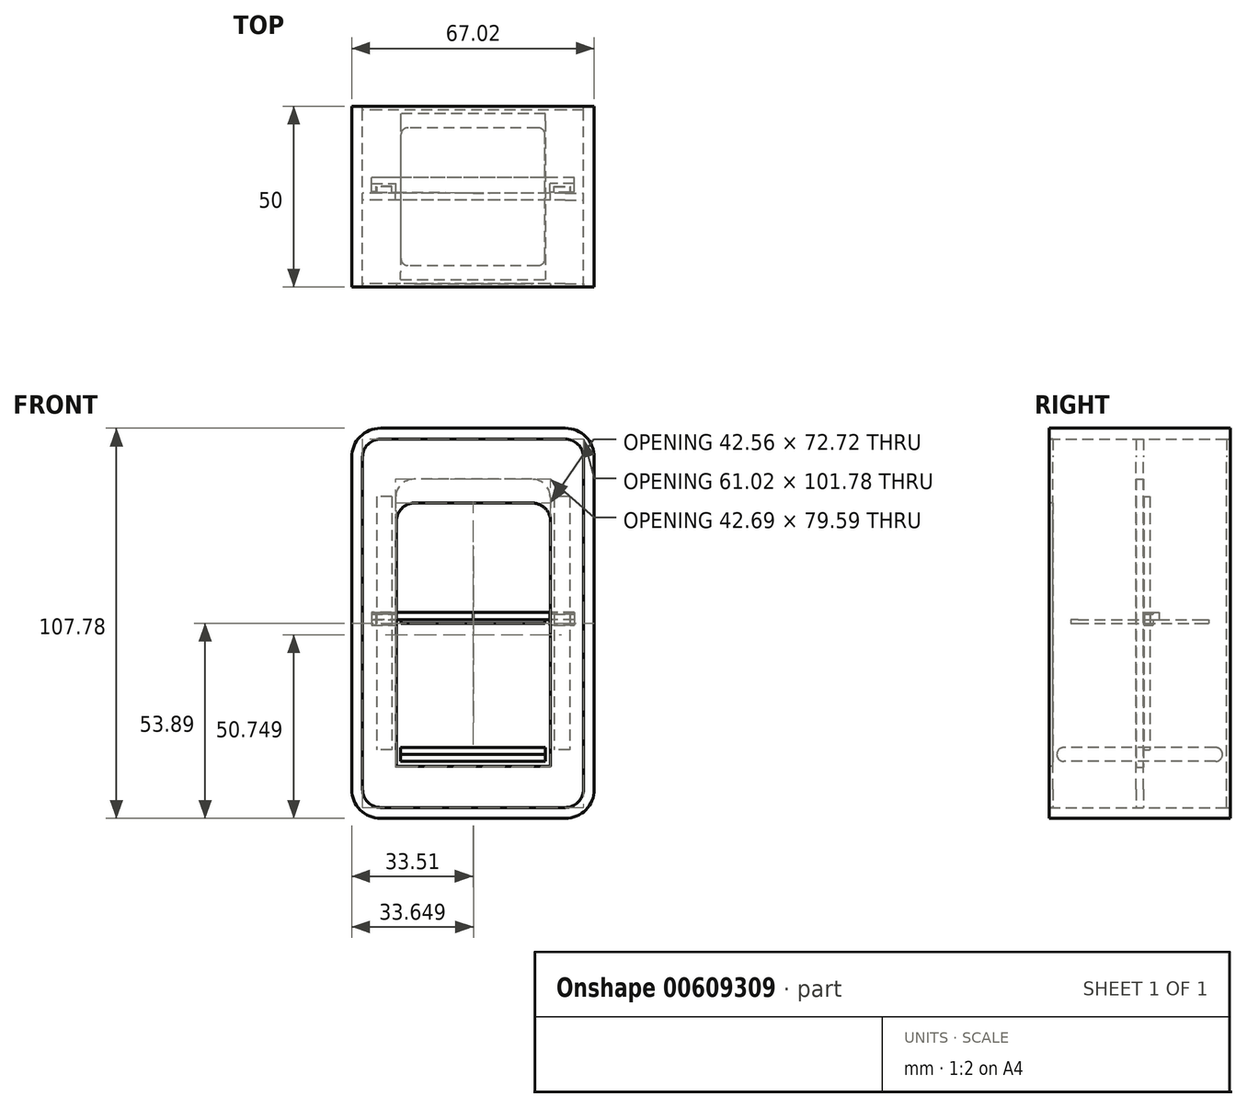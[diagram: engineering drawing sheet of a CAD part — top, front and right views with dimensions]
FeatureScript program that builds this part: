
annotation { "Feature Type Name" : "Feature", "Feature Type Description" : "" }
export const myFeature = defineFeature(function(context is Context, id is Id, definition is map)
    precondition{}
    {
        {
            var Q0;
            Q0=qCreatedBy(makeId("Front.planeOp"),FACE);
            var sketch = newSketch(context, id + "F0", { "sketchPlane" : qUnion([Q0])});
            skLineSegment(sketch, "E0.bottom", {"start": v(25.51, -50.9) * mm, "end": v(-25.51, -50.9) * mm});
            skLineSegment(sketch, "E0.top", {"start": v(25.51, 50.9) * mm, "end": v(-25.51, 50.9) * mm});
            skLineSegment(sketch, "E0.left", {"start": v(30.51, -45.9) * mm, "end": v(30.51, 45.9) * mm});
            skLineSegment(sketch, "E0.right", {"start": v(-30.51, -45.9) * mm, "end": v(-30.51, 45.9) * mm});
            skPoint(sketch, "E0.middle", {"position": v(0, 0) * mm});
            skLineSegment(sketch, "E1.bottom", {"start": v(16.35, 39.8) * mm, "end": v(-16.35, 39.8) * mm});
            skLineSegment(sketch, "E1.top", {"start": v(21.35, -39.8) * mm, "end": v(-21.35, -39.8) * mm});
            skLineSegment(sketch, "E1.left", {"start": v(21.35, 34.8) * mm, "end": v(21.35, -39.8) * mm});
            skLineSegment(sketch, "E1.right", {"start": v(-21.35, 34.8) * mm, "end": v(-21.35, -39.8) * mm});
            skPoint(sketch, "E2.visualSharp", {"position": v(-30.51, 50.9) * mm});
            skArc(sketch, "E2.filletArc", {"start": v(-25.51, 50.9) * mm, "mid": v(-29.05, 49.43) * mm, "end": v(-30.51, 45.9) * mm});
            skPoint(sketch, "E3.visualSharp", {"position": v(30.51, 50.9) * mm});
            skArc(sketch, "E3.filletArc", {"start": v(30.51, 45.9) * mm, "mid": v(29.05, 49.43) * mm, "end": v(25.51, 50.9) * mm});
            skPoint(sketch, "E4.visualSharp", {"position": v(-30.51, -50.9) * mm});
            skArc(sketch, "E4.filletArc", {"start": v(-30.51, -45.9) * mm, "mid": v(-29.05, -49.43) * mm, "end": v(-25.51, -50.9) * mm});
            skPoint(sketch, "E5.visualSharp", {"position": v(30.51, -50.9) * mm});
            skArc(sketch, "E5.filletArc", {"start": v(25.51, -50.9) * mm, "mid": v(29.05, -49.43) * mm, "end": v(30.51, -45.9) * mm});
            skPoint(sketch, "E6.visualSharp", {"position": v(-21.35, 39.8) * mm});
            skArc(sketch, "E6.filletArc", {"start": v(-16.35, 39.8) * mm, "mid": v(-19.88, 38.33) * mm, "end": v(-21.35, 34.8) * mm});
            skPoint(sketch, "E7.visualSharp", {"position": v(21.35, 39.8) * mm});
            skArc(sketch, "E7.filletArc", {"start": v(21.35, 34.8) * mm, "mid": v(19.88, 38.33) * mm, "end": v(16.35, 39.8) * mm});
            skArc(sketch, "E8.0", {"start": v(33.51, 45.9) * mm, "mid": v(31.17, 51.55) * mm, "end": v(25.51, 53.9) * mm});
            skLineSegment(sketch, "E8.1", {"start": v(33.51, -45.9) * mm, "end": v(33.51, 45.9) * mm});
            skLineSegment(sketch, "E8.2", {"start": v(25.51, 53.9) * mm, "end": v(-25.51, 53.9) * mm});
            skArc(sketch, "E8.3", {"start": v(25.51, -53.9) * mm, "mid": v(31.17, -51.55) * mm, "end": v(33.51, -45.9) * mm});
            skArc(sketch, "E8.4", {"start": v(-25.51, 53.9) * mm, "mid": v(-31.17, 51.55) * mm, "end": v(-33.51, 45.9) * mm});
            skLineSegment(sketch, "E8.5", {"start": v(-33.51, -45.9) * mm, "end": v(-33.51, 45.9) * mm});
            skArc(sketch, "E8.6", {"start": v(-33.51, -45.9) * mm, "mid": v(-31.17, -51.55) * mm, "end": v(-25.51, -53.9) * mm});
            skLineSegment(sketch, "E8.7", {"start": v(25.51, -53.9) * mm, "end": v(-25.51, -53.9) * mm});
            skSolve(sketch);
        }
        {
            var Q0;
            Q0=makeQuery(id+"F0.imprint","IMPRINT",FACE,{"disambiguationData":[TD([[makeQuery(id+"F0.imprint","IMPRINT",EDGE,{"derivedFrom":sQuery(id+"F0.wireOp",EDGE,"E0.bottom")}),-1.0]])]});
            extrude(context, id + "F1", {"entities" : qUnion([Q0]), "endBound" : BoundingType.SYMMETRIC, "depth" : 2 * mm, "offsetDistance" : 25 * mm});
        }
        {
            var Q0;
            Q0 = qSketchRegion(id + "F0", true);
            extrude(context, id + "F2", {"entities" : qUnion([Q0]), "endBound" : BoundingType.SYMMETRIC, "depth" : 50 * mm, "offsetDistance" : 25 * mm});
        }
        {
            var Q0;
            Q0=makeQuery(id+"F2.opExtrude","CAP_FACE",FACE,{"disambiguationData":[OSD([sQuery(id+"F0.wireOp",EDGE,"E0.bottom"),sQuery(id+"F0.wireOp",EDGE,"E0.top"),sQuery(id+"F0.wireOp",EDGE,"E0.left"),sQuery(id+"F0.wireOp",EDGE,"E0.right"),sQuery(id+"F0.wireOp",EDGE,"E2.filletArc"),sQuery(id+"F0.wireOp",EDGE,"E3.filletArc"),sQuery(id+"F0.wireOp",EDGE,"E4.filletArc"),sQuery(id+"F0.wireOp",EDGE,"E5.filletArc"),sQuery(id+"F0.wireOp",EDGE,"E8.0"),sQuery(id+"F0.wireOp",EDGE,"E8.1"),sQuery(id+"F0.wireOp",EDGE,"E8.2"),sQuery(id+"F0.wireOp",EDGE,"E8.3"),sQuery(id+"F0.wireOp",EDGE,"E8.4"),sQuery(id+"F0.wireOp",EDGE,"E8.5"),sQuery(id+"F0.wireOp",EDGE,"E8.6"),sQuery(id+"F0.wireOp",EDGE,"E8.7")])],"isStart":false});
            var sketch = newSketch(context, id + "F3", { "sketchPlane" : qUnion([Q0])});
            skLineSegment(sketch, "E9.bottom", {"start": v(25.51, 50.9) * mm, "end": v(-25.51, 50.9) * mm});
            skLineSegment(sketch, "E9.top", {"start": v(25.51, -50.9) * mm, "end": v(-25.51, -50.9) * mm});
            skLineSegment(sketch, "E9.left", {"start": v(30.51, 45.9) * mm, "end": v(30.51, -45.9) * mm});
            skLineSegment(sketch, "E9.right", {"start": v(-30.51, 45.9) * mm, "end": v(-30.51, -45.9) * mm});
            skPoint(sketch, "E9.middle", {"position": v(0, 0) * mm});
            skPoint(sketch, "E10.visualSharp", {"position": v(-30.51, 50.9) * mm});
            skArc(sketch, "E10.filletArc", {"start": v(-25.51, 50.9) * mm, "mid": v(-29.05, 49.43) * mm, "end": v(-30.51, 45.9) * mm});
            skPoint(sketch, "E11.visualSharp", {"position": v(30.51, 50.9) * mm});
            skArc(sketch, "E11.filletArc", {"start": v(30.51, 45.9) * mm, "mid": v(29.05, 49.43) * mm, "end": v(25.51, 50.9) * mm});
            skPoint(sketch, "E12.visualSharp", {"position": v(30.51, -50.9) * mm});
            skArc(sketch, "E12.filletArc", {"start": v(25.51, -50.9) * mm, "mid": v(29.05, -49.43) * mm, "end": v(30.51, -45.9) * mm});
            skPoint(sketch, "E13.visualSharp", {"position": v(-30.51, -50.9) * mm});
            skArc(sketch, "E13.filletArc", {"start": v(-30.51, -45.9) * mm, "mid": v(-29.05, -49.43) * mm, "end": v(-25.51, -50.9) * mm});
            skLineSegment(sketch, "E14", {"start": v(21.35, 19.84) * mm, "end": v(21.35, -39.5) * mm});
            skLineSegment(sketch, "E15", {"start": v(21.35, -39.5) * mm, "end": v(-21.14, -39.5) * mm});
            skLineSegment(sketch, "E16", {"start": v(-21.14, -39.5) * mm, "end": v(-21.14, 19.84) * mm});
            skPoint(sketch, "E17.start.orphan", {"position": v(0, 50.9) * mm});
            skPoint(sketch, "E18.visualSharp", {"position": v(-21.14, 24.84) * mm});
            skPoint(sketch, "E19.visualSharp", {"position": v(21.35, 24.84) * mm});
            skLineSegment(sketch, "E20", {"start": v(-21.14, 19.84) * mm, "end": v(-21.14, 28.22) * mm});
            skLineSegment(sketch, "E21", {"start": v(-16.14, 33.22) * mm, "end": v(16.42, 33.22) * mm});
            skLineSegment(sketch, "E22", {"start": v(21.42, 28.18) * mm, "end": v(21.35, 19.84) * mm});
            skPoint(sketch, "E23.visualSharp", {"position": v(-21.14, 33.22) * mm});
            skArc(sketch, "E23.filletArc", {"start": v(-16.14, 33.22) * mm, "mid": v(-19.68, 31.76) * mm, "end": v(-21.14, 28.22) * mm});
            skPoint(sketch, "E24.visualSharp", {"position": v(21.46, 33.22) * mm});
            skArc(sketch, "E24.filletArc", {"start": v(21.42, 28.18) * mm, "mid": v(19.97, 31.74) * mm, "end": v(16.42, 33.22) * mm});
            skPoint(sketch, "E25.start.orphan", {"position": v(0, 24.84) * mm});
            skSolve(sketch);
        }
        {
            var Q0;
            Q0=makeQuery(id+"F3.imprint","IMPRINT",FACE,{"disambiguationData":[TD([[makeQuery(id+"F3.imprint","IMPRINT",EDGE,{"derivedFrom":sQuery(id+"F3.wireOp",EDGE,"E9.bottom")}),1.0]])]});
            extrude(context, id + "F4", {"entities" : qUnion([Q0]), "oppositeDirection" : true, "depth" : 1 * mm, "offsetDistance" : 25 * mm});
        }
        {
            var Q0;
            Q0=makeQuery(id+"F2.opExtrude","CAP_FACE",FACE,{"disambiguationData":[OSD([sQuery(id+"F0.wireOp",EDGE,"E0.bottom"),sQuery(id+"F0.wireOp",EDGE,"E0.top"),sQuery(id+"F0.wireOp",EDGE,"E0.left"),sQuery(id+"F0.wireOp",EDGE,"E0.right"),sQuery(id+"F0.wireOp",EDGE,"E2.filletArc"),sQuery(id+"F0.wireOp",EDGE,"E3.filletArc"),sQuery(id+"F0.wireOp",EDGE,"E4.filletArc"),sQuery(id+"F0.wireOp",EDGE,"E5.filletArc"),sQuery(id+"F0.wireOp",EDGE,"E8.0"),sQuery(id+"F0.wireOp",EDGE,"E8.1"),sQuery(id+"F0.wireOp",EDGE,"E8.2"),sQuery(id+"F0.wireOp",EDGE,"E8.3"),sQuery(id+"F0.wireOp",EDGE,"E8.4"),sQuery(id+"F0.wireOp",EDGE,"E8.5"),sQuery(id+"F0.wireOp",EDGE,"E8.6"),sQuery(id+"F0.wireOp",EDGE,"E8.7")])],"isStart":true});
            var sketch = newSketch(context, id + "F5", { "sketchPlane" : qUnion([Q0])});
            skLineSegment(sketch, "E26.bottom", {"start": v(25.51, 50.9) * mm, "end": v(-25.51, 50.9) * mm});
            skLineSegment(sketch, "E26.top", {"start": v(25.51, -50.9) * mm, "end": v(-25.51, -50.9) * mm});
            skLineSegment(sketch, "E26.left", {"start": v(30.51, 45.9) * mm, "end": v(30.51, -45.9) * mm});
            skLineSegment(sketch, "E26.right", {"start": v(-30.51, 45.9) * mm, "end": v(-30.51, -45.9) * mm});
            skPoint(sketch, "E26.middle", {"position": v(0, 0) * mm});
            skPoint(sketch, "E27.visualSharp", {"position": v(-30.51, 50.9) * mm});
            skArc(sketch, "E27.filletArc", {"start": v(-25.51, 50.9) * mm, "mid": v(-29.05, 49.43) * mm, "end": v(-30.51, 45.9) * mm});
            skPoint(sketch, "E28.visualSharp", {"position": v(30.51, 50.9) * mm});
            skArc(sketch, "E28.filletArc", {"start": v(30.51, 45.9) * mm, "mid": v(29.05, 49.43) * mm, "end": v(25.51, 50.9) * mm});
            skPoint(sketch, "E29.visualSharp", {"position": v(30.51, -50.9) * mm});
            skArc(sketch, "E29.filletArc", {"start": v(25.51, -50.9) * mm, "mid": v(29.05, -49.43) * mm, "end": v(30.51, -45.9) * mm});
            skPoint(sketch, "E30.visualSharp", {"position": v(-30.51, -50.9) * mm});
            skArc(sketch, "E30.filletArc", {"start": v(-30.51, -45.9) * mm, "mid": v(-29.05, -49.43) * mm, "end": v(-25.51, -50.9) * mm});
            skSolve(sketch);
        }
        {
            var Q0;
            Q0 = qSketchRegion(id + "F5", true);
            extrude(context, id + "F6", {"entities" : qUnion([Q0]), "oppositeDirection" : true, "depth" : 1 * mm, "offsetDistance" : 25 * mm});
        }
        {
            var Q0;
            Q0=qCreatedBy(makeId("Right.planeOp"),FACE);
            var sketch = newSketch(context, id + "F7", { "sketchPlane" : qUnion([Q0])});
            skLineSegment(sketch, "E31", {"start": v(0, -38.17) * mm, "end": v(-22.91, -38.17) * mm});
            skLineSegment(sketch, "E32", {"start": v(-22.91, -38.17) * mm, "end": v(-22.91, -34.3) * mm});
            skLineSegment(sketch, "E33", {"start": v(-22.91, -34.3) * mm, "end": v(0, -34.3) * mm});
            skLineSegment(sketch, "E34.MirrorCS", {"start": v(22.91, -34.3) * mm, "end": v(0, -34.3) * mm});
            skLineSegment(sketch, "E35.MirrorCS", {"start": v(0, -38.17) * mm, "end": v(22.91, -38.17) * mm});
            skLineSegment(sketch, "E36.MirrorCS", {"start": v(22.91, -38.17) * mm, "end": v(22.91, -34.3) * mm});
            skPoint(sketch, "E37.start.orphan", {"position": v(0, -39.6) * mm});
            skSolve(sketch);
        }
        {
            var Q0;
            Q0=makeQuery(id+"F7.imprint","IMPRINT",FACE,{"disambiguationData":[TD([[makeQuery(id+"F7.imprint","IMPRINT",EDGE,{"derivedFrom":sQuery(id+"F7.wireOp",EDGE,"E31")}),-1.0]])]});
            extrude(context, id + "F8", {"entities" : qUnion([Q0]), "endBound" : BoundingType.SYMMETRIC, "depth" : 40 * mm, "offsetDistance" : 25 * mm});
        }
        {
            var Q0;
            Q0=makeQuery(id+"F8.opExtrude","SWEPT_EDGE",EDGE,{"disambiguationData":[OSD([sQuery(id+"F7.wireOp",EDGE,"E32"),sQuery(id+"F7.wireOp",EDGE,"E33")])]});
            var Q1;
            Q1=makeQuery(id+"F8.opExtrude","SWEPT_EDGE",EDGE,{"disambiguationData":[OSD([sQuery(id+"F7.wireOp",EDGE,"E31"),sQuery(id+"F7.wireOp",EDGE,"E32")])]});
            var Q2;
            Q2=makeQuery(id+"F8.opExtrude","SWEPT_EDGE",EDGE,{"disambiguationData":[OSD([sQuery(id+"F7.wireOp",EDGE,"E34.MirrorCS"),sQuery(id+"F7.wireOp",EDGE,"E36.MirrorCS")])]});
            var Q3;
            Q3=makeQuery(id+"F8.opExtrude","SWEPT_EDGE",EDGE,{"disambiguationData":[OSD([sQuery(id+"F7.wireOp",EDGE,"E35.MirrorCS"),sQuery(id+"F7.wireOp",EDGE,"E36.MirrorCS")])]});
            fillet(context, id + "F9", {"entities" : qUnion([Q0, Q1, Q2, Q3]), "radius" : 2 * mm, "tangentPropagation" : true, "allowEdgeOverflow" : false});
        }
        {
            var Q0;
            Q0=qCreatedBy(makeId("Top.planeOp"),FACE);
            var sketch = newSketch(context, id + "F10", { "sketchPlane" : qUnion([Q0])});
            skLineSegment(sketch, "E38", {"start": v(22.43, 1.18) * mm, "end": v(22.43, 2.77) * mm});
            skLineSegment(sketch, "E39", {"start": v(22.43, 2.77) * mm, "end": v(26.66, 2.77) * mm});
            skLineSegment(sketch, "E40", {"start": v(26.66, 2.77) * mm, "end": v(26.66, 1.18) * mm});
            skLineSegment(sketch, "E41", {"start": v(26.66, 1.18) * mm, "end": v(22.43, 1.18) * mm});
            skLineSegment(sketch, "E42.MirrorCS", {"start": v(-22.43, 2.77) * mm, "end": v(-26.66, 2.77) * mm});
            skLineSegment(sketch, "E43.MirrorCS", {"start": v(-22.43, 1.18) * mm, "end": v(-22.43, 2.77) * mm});
            skLineSegment(sketch, "E44.MirrorCS", {"start": v(-26.66, 1.18) * mm, "end": v(-22.43, 1.18) * mm});
            skLineSegment(sketch, "E45.MirrorCS", {"start": v(-26.66, 2.77) * mm, "end": v(-26.66, 1.18) * mm});
            skSolve(sketch);
        }
        {
            var Q0;
            Q0=makeQuery(id+"F10.imprint","IMPRINT",FACE,{"disambiguationData":[TD([[makeQuery(id+"F10.imprint","IMPRINT",EDGE,{"derivedFrom":sQuery(id+"F10.wireOp",EDGE,"E38")}),-1.0]])]});
            var Q1;
            Q1=makeQuery(id+"F10.imprint","IMPRINT",FACE,{"disambiguationData":[TD([[makeQuery(id+"F10.imprint","IMPRINT",EDGE,{"derivedFrom":sQuery(id+"F10.wireOp",EDGE,"E42.MirrorCS")}),1.0]])]});
            extrude(context, id + "F11", {"entities" : qUnion([Q0, Q1]), "endBound" : BoundingType.SYMMETRIC, "depth" : 70 * mm, "offsetDistance" : 25 * mm});
        }
        {
            var Q0;
            Q0=qCreatedBy(makeId("Top.planeOp"),FACE);
            var sketch = newSketch(context, id + "F12", { "sketchPlane" : qUnion([Q0])});
            skLineSegment(sketch, "E46.bottom", {"start": v(19.9, -19.05) * mm, "end": v(-19.9, -19.05) * mm});
            skLineSegment(sketch, "E46.top", {"start": v(19.9, 19.05) * mm, "end": v(-19.9, 19.05) * mm});
            skLineSegment(sketch, "E46.left", {"start": v(19.9, -19.05) * mm, "end": v(19.9, 19.05) * mm});
            skLineSegment(sketch, "E46.right", {"start": v(-19.9, -19.05) * mm, "end": v(-19.9, 19.05) * mm});
            skPoint(sketch, "E46.middle", {"position": v(0, 0) * mm});
            skSolve(sketch);
        }
        {
            var Q0;
            Q0=makeQuery(id+"F12.imprint","IMPRINT",FACE,{"disambiguationData":[TD([[makeQuery(id+"F12.imprint","IMPRINT",EDGE,{"derivedFrom":sQuery(id+"F12.wireOp",EDGE,"E46.bottom")}),-1.0]])]});
            extrude(context, id + "F13", {"entities" : qUnion([Q0]), "depth" : 1 * mm, "offsetDistance" : 25 * mm});
        }
        {
            var Q0;
            Q0=makeQuery(id+"F13.opExtrude","SWEPT_EDGE",EDGE,{"disambiguationData":[OSD([sQuery(id+"F12.wireOp",EDGE,"E46.bottom"),sQuery(id+"F12.wireOp",EDGE,"E46.left")])]});
            var Q1;
            Q1=makeQuery(id+"F13.opExtrude","SWEPT_EDGE",EDGE,{"disambiguationData":[OSD([sQuery(id+"F12.wireOp",EDGE,"E46.bottom"),sQuery(id+"F12.wireOp",EDGE,"E46.right")])]});
            var Q2;
            Q2=makeQuery(id+"F13.opExtrude","SWEPT_EDGE",EDGE,{"disambiguationData":[OSD([sQuery(id+"F12.wireOp",EDGE,"E46.top"),sQuery(id+"F12.wireOp",EDGE,"E46.right")])]});
            var Q3;
            Q3=makeQuery(id+"F13.opExtrude","SWEPT_EDGE",EDGE,{"disambiguationData":[OSD([sQuery(id+"F12.wireOp",EDGE,"E46.top"),sQuery(id+"F12.wireOp",EDGE,"E46.left")])]});
            fillet(context, id + "F14", {"entities" : qUnion([Q0, Q1, Q2, Q3]), "radius" : 2 * mm, "tangentPropagation" : true, "allowEdgeOverflow" : false});
        }
        {
            var Q0;
            Q0=makeQuery(id+"F13.opExtrude","CAP_FACE",FACE,{"disambiguationData":[OSD([sQuery(id+"F12.wireOp",EDGE,"E46.bottom"),sQuery(id+"F12.wireOp",EDGE,"E46.top"),sQuery(id+"F12.wireOp",EDGE,"E46.left"),sQuery(id+"F12.wireOp",EDGE,"E46.right")])],"isStart":false});
            var sketch = newSketch(context, id + "F15", { "sketchPlane" : qUnion([Q0])});
            skLineSegment(sketch, "E47", {"start": v(-22.41, 1.16) * mm, "end": v(-21.26, 1.16) * mm});
            skLineSegment(sketch, "E48", {"start": v(-21.26, 1.16) * mm, "end": v(-21.26, 3.66) * mm});
            skLineSegment(sketch, "E49", {"start": v(-26.84, 1.28) * mm, "end": v(-28, 1.28) * mm});
            skLineSegment(sketch, "E50", {"start": v(-28, 1.28) * mm, "end": v(-28, 3.66) * mm});
            skLineSegment(sketch, "E51", {"start": v(-28, 3.66) * mm, "end": v(-21.26, 3.66) * mm});
            skLineSegment(sketch, "E52", {"start": v(-22.41, 1.16) * mm, "end": v(-22.41, 2.88) * mm});
            skLineSegment(sketch, "E53", {"start": v(-22.41, 2.88) * mm, "end": v(-26.84, 2.88) * mm});
            skLineSegment(sketch, "E54", {"start": v(-26.84, 2.88) * mm, "end": v(-26.84, 1.28) * mm});
            skLineSegment(sketch, "E55", {"start": v(-28, 3.66) * mm, "end": v(-28, 5.32) * mm});
            skLineSegment(sketch, "E56", {"start": v(-28, 5.32) * mm, "end": v(0, 5.32) * mm});
            skLineSegment(sketch, "E57", {"start": v(0, 5.32) * mm, "end": v(0, 0.94) * mm});
            skLineSegment(sketch, "E58", {"start": v(0, 0.94) * mm, "end": v(-21.26, 1.16) * mm});
            skLineSegment(sketch, "E59.MirrorCS", {"start": v(28, 5.32) * mm, "end": v(0, 5.32) * mm});
            skLineSegment(sketch, "E60.MirrorCS", {"start": v(28, 3.66) * mm, "end": v(28, 5.32) * mm});
            skLineSegment(sketch, "E61.MirrorCS", {"start": v(26.84, 1.28) * mm, "end": v(28, 1.28) * mm});
            skLineSegment(sketch, "E62.MirrorCS", {"start": v(22.41, 1.16) * mm, "end": v(21.26, 1.16) * mm});
            skLineSegment(sketch, "E63.MirrorCS", {"start": v(26.84, 2.88) * mm, "end": v(26.84, 1.28) * mm});
            skLineSegment(sketch, "E64.MirrorCS", {"start": v(22.41, 2.88) * mm, "end": v(26.84, 2.88) * mm});
            skLineSegment(sketch, "E65.MirrorCS", {"start": v(22.41, 1.16) * mm, "end": v(22.41, 2.88) * mm});
            skLineSegment(sketch, "E66.MirrorCS", {"start": v(28, 3.66) * mm, "end": v(21.26, 3.66) * mm});
            skLineSegment(sketch, "E67.MirrorCS", {"start": v(28, 1.28) * mm, "end": v(28, 3.66) * mm});
            skLineSegment(sketch, "E68.MirrorCS", {"start": v(21.26, 1.16) * mm, "end": v(21.26, 3.66) * mm});
            skLineSegment(sketch, "E69.MirrorCS", {"start": v(0, 0.94) * mm, "end": v(21.26, 1.16) * mm});
            skSolve(sketch);
        }
        {
            var Q0;
            {var subQ6=sQuery(id+"F15.wireOp",EDGE,"E60.MirrorCS");Q0=makeQuery(id+"F15.imprint","IMPRINT",FACE,{"disambiguationData":[TD([[makeQuery(id+"F15.imprint","IMPRINT",EDGE,{"derivedFrom":subQ6}),1.0]])]});}
            var Q1;
            {var subQ0=sQuery(id+"F15.wireOp",EDGE,"E57");Q1=makeQuery(id+"F15.imprint","IMPRINT",FACE,{"disambiguationData":[TD([[makeQuery(id+"F15.imprint","IMPRINT",EDGE,{"derivedFrom":subQ0}),1.0]])]});}
            var Q2;
            {var subQ0=sQuery(id+"F15.wireOp",EDGE,"E57");Q2=makeQuery(id+"F15.imprint","IMPRINT",FACE,{"disambiguationData":[TD([[makeQuery(id+"F15.imprint","IMPRINT",EDGE,{"derivedFrom":subQ0}),-1.0]])]});}
            var Q3;
            {var subQ4=sQuery(id+"F15.wireOp",EDGE,"E48");Q3=makeQuery(id+"F15.imprint","IMPRINT",FACE,{"disambiguationData":[TD([[makeQuery(id+"F15.imprint","IMPRINT",EDGE,{"derivedFrom":subQ4}),-1.0]])]});}
            extrude(context, id + "F16", {"entities" : qUnion([Q0, Q1, Q2, Q3]), "operationType" : NewBodyOperationType.ADD, "depth" : 2 * mm, "offsetDistance" : 25 * mm});
        }
        {
            var Q0;
            Q0=makeQuery(id+"F15.imprint","IMPRINT",FACE,{"disambiguationData":[TD([[makeQuery(id+"F15.imprint","IMPRINT",EDGE,{"derivedFrom":sQuery(id+"F15.wireOp",EDGE,"E47")}),1.0]])]});
            var Q1;
            Q1=makeQuery(id+"F15.imprint","IMPRINT",FACE,{"disambiguationData":[TD([[makeQuery(id+"F15.imprint","IMPRINT",EDGE,{"derivedFrom":sQuery(id+"F15.wireOp",EDGE,"E61.MirrorCS")}),1.0]])]});
            extrude(context, id + "F17", {"entities" : qUnion([Q0, Q1]), "operationType" : NewBodyOperationType.ADD, "endBound" : BoundingType.SYMMETRIC, "depth" : 3 * mm, "offsetDistance" : 25 * mm});
        }
    });
